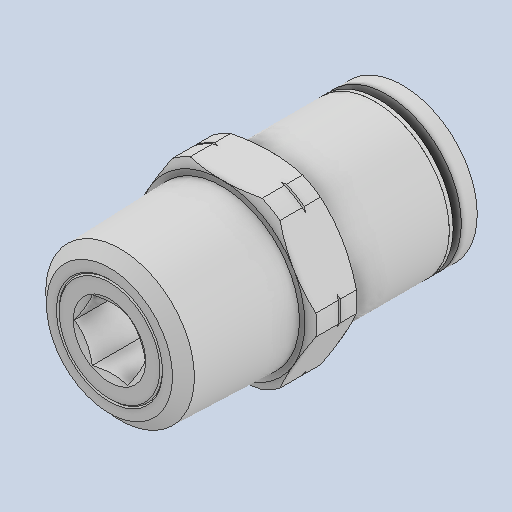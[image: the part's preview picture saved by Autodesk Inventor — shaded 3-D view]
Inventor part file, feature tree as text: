
AUTODESK INVENTOR PART (.ipt)
format: ipt  version: 2025 (Build 290162000, 162)  size: 253,952 bytes
history: native  units: mm
features: other x3, chamfer x1
ambient origin geometry x8: Origin, YZ Plane, XZ Plane, XY Plane, X Axis, Y Axis, Z Axis, Center Point
bodies: Solid1 (feature_tree), Solid2 (feature_tree), Solid3 (feature_tree), Solid4 (feature_tree)
feature tree (4):
  chamfer  "Chamfer4"  [1 undecoded]
  other  "Cut-Extrude8"
  other  "Boss-Extrude4"
  other  "Cut-Revolve1"
note: 1 required parameter value undecoded (feature->parameter linkage not recoverable at this tier; creation-order binding heuristic only, values carry confidence <= 0.55)
